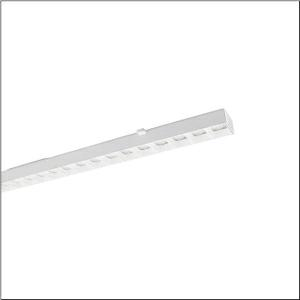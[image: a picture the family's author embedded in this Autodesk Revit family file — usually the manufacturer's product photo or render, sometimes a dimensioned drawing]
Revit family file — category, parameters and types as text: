
# Revit family: silica_r__31_fur_modario_r__31_51ry1tmb46c_60a4
name_source: partatom
category: Lighting Fixtures
units: mm (PartAtom-declared; Revit-internal decimal feet)

## family parameters
Cut with Voids When Loaded = No
Host = Face
Light Source = No
Part Type = Normal
Room Calculation Point = No
Round Connector Dimension = Use Diameter
Shared = No

## types (1)
- --- (1 x LED, 6710 lm, 37.8 W, 4000K)
    Apparent Load = 38 VA
    CIE Flux Codes = 84 98 100 100 100
    Color Rendering = 80
    Color Temperature = 4000K
    Default Elevation = 1800 mm
    Description = Silica® 31 for Modario® 31, luminaire insert, of aluminium, coated, traffic white (RAL 9016), length: 1.495mm, width: 79mm, height: 62mm, 5x system unit, system units: 299mm, LED rated luminous flux: 6.710lm, light colour: 840, control gear: ON/OFF Multilumen, with system connector: socket, mains connection: 220..240V, AC, 50/60Hz, rated input power: 38W, luminous flux adjustable on luminaire in four steps (3920/4730/5690/6710lm), connected load according to luminous flux setting (21.7/26.3/31.8/37.8W), primary light control with lens, of PMMA, primary anti-glare with reflector, of PC, CAT 2 (L<= 3000cd/m²), light emission: direct distribution, primary light characteristic: symmetric, protection rating (complete): IP20, insulation class (complete): insulation class I (protective earthing), certification: CE, UKCA, impact resistance: IK02, permissible ambient temperature for indoor applications: -20..+40°C, LABS conformity tested according to VDMA 24364:2018-05, packaging unit: 1 piece
    Height = 62 mm  [stored 0.203412 ft]
    Lamp = 1 x LED
    Lamp Light Flux = 6710 lm
    Lamp Power = 37.8 W
    Lamp count = 1
    Length = 1495 mm
    Luminous efficacy = 178 lm/W
    Manufacturer = Siteco
    ModVariant = No
    Model = 51RY1TMB46C
    Mounting Place = Ceiling
    Mounting Type = Pendant
    Number of Poles = 1
    OnlyDefault = Yes
    Power Factor = 1
    Product Name = Silica® 31 für Modario® 31
    Product group = luminaire insert
    ProductGroupID = 901
    Protection Class = Protection class I
    Protection Degree = IP 20
    RLX_Detail_Level = 1
    RLX_Emergency_Light_Flux = 0 lm
    RLX_Emergency_Type = 0
    RLX_Emergency_Type_DB = No
    RlxData = <blob elided: 14097 chars, md5=86629763>
    Socket = socket
    Standby Power = 0 W
    System Light Flux = 6710 lm
    System Power = 38 W
    Type Comments = factory setting: luminous flux: 100 % | (OFF | OFF | OFF) | 350 mA
    Type Image = l_1299352.jpg
    URL = http://relux.com
    VarID = @adj_017189
    Voltage = 0 V
    Weight = 0.00 kg
    Width = 79 mm

note: [stored X ft] marks values corroborated as IEEE doubles in the binary element streams (Revit-internal decimal feet)

## geometry (parser evidence)
native form markers: Sweep x10
no freeform markers — native parametric forms only
